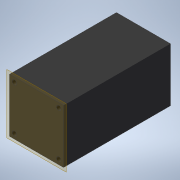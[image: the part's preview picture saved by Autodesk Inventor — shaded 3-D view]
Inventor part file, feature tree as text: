
AUTODESK INVENTOR PART (.ipt)
format: ipt  version: 2020 (Build 240168000, 168)  size: 103,936 bytes
history: native  units: mm
features: extrude x1, sketch x1
ambient origin geometry x8: Origin, YZ Plane, XZ Plane, XY Plane, X Axis, Y Axis, Z Axis, Center Point
bodies: Solid1 (feature_tree)
feature tree (2):
  extrude  "Extrusion1"  Depth=57.0mm
  sketch  "Sketch1"  dims[d0=57.0mm d1=57.0mm d2=5.0mm d3=5.0mm d4=5.0mm d5=113.0mm d6=0.0mm]
